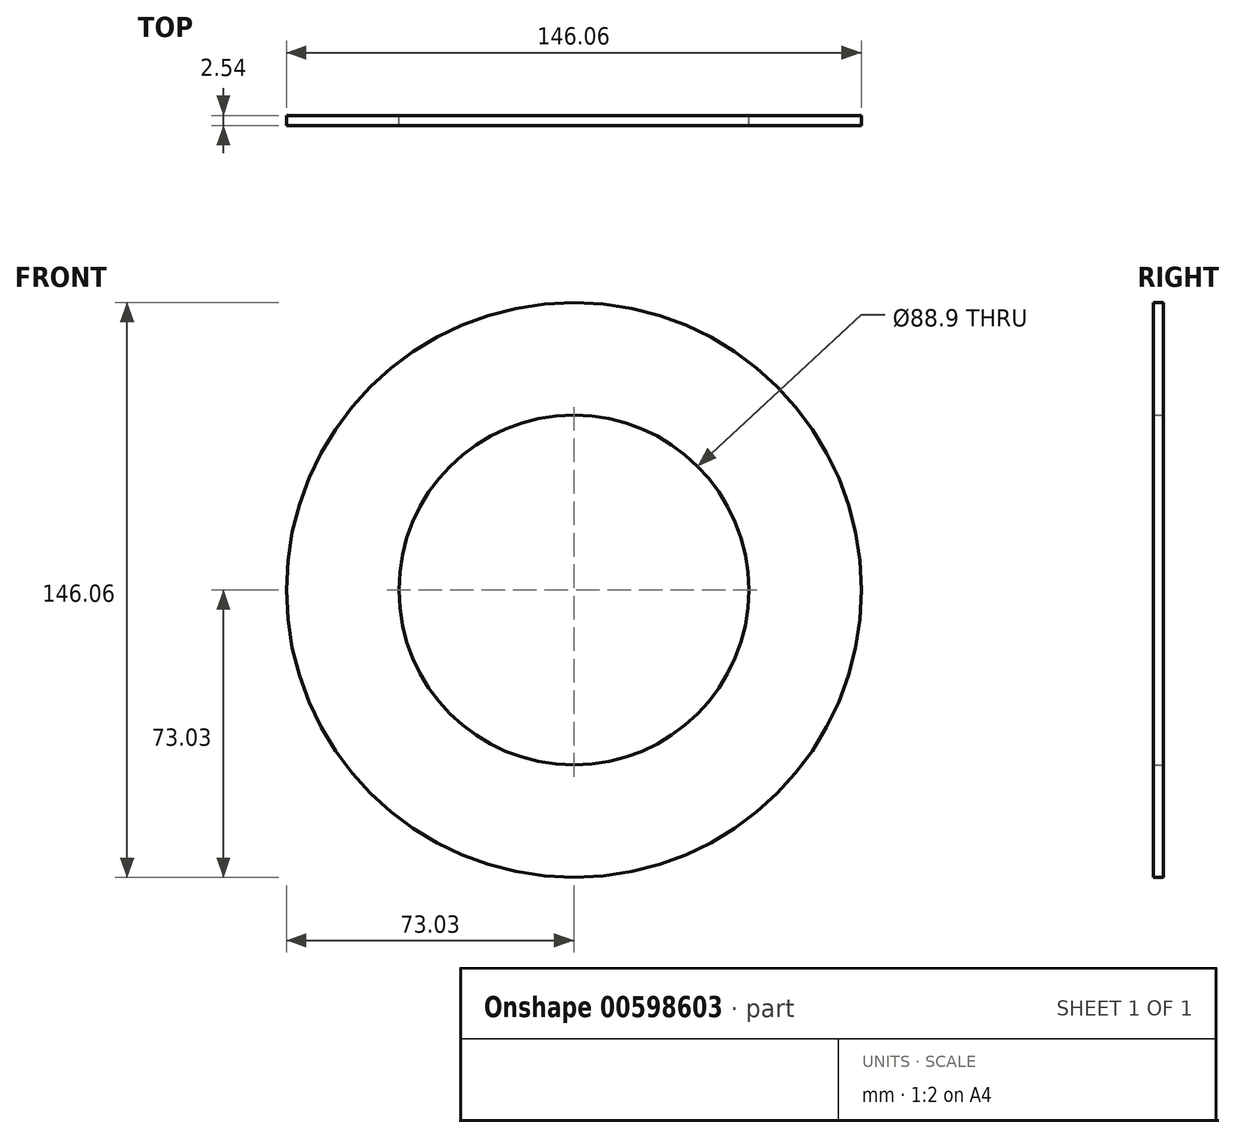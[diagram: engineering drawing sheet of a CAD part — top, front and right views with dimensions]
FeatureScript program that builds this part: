
annotation { "Feature Type Name" : "Feature", "Feature Type Description" : "" }
export const myFeature = defineFeature(function(context is Context, id is Id, definition is map)
    precondition{}
    {
        {
            var Q0;
            Q0=qCreatedBy(makeId("Front.planeOp"),FACE);
            var sketch = newSketch(context, id + "F0", { "sketchPlane" : qUnion([Q0])});
            skCircle(sketch, "E0", {"center": v(0, 0) * mm, "radius": 73.03 * mm});
            skCircle(sketch, "E1", {"center": v(0, 0) * mm, "radius": 44.45 * mm});
            skSolve(sketch);
        }
        {
            var Q0;
            Q0 = qSketchRegion(id + "F0", true);
            extrude(context, id + "F1", {"entities" : qUnion([Q0]), "depth" : 2.54 * mm, "offsetDistance" : 25.4 * mm});
        }
    });
